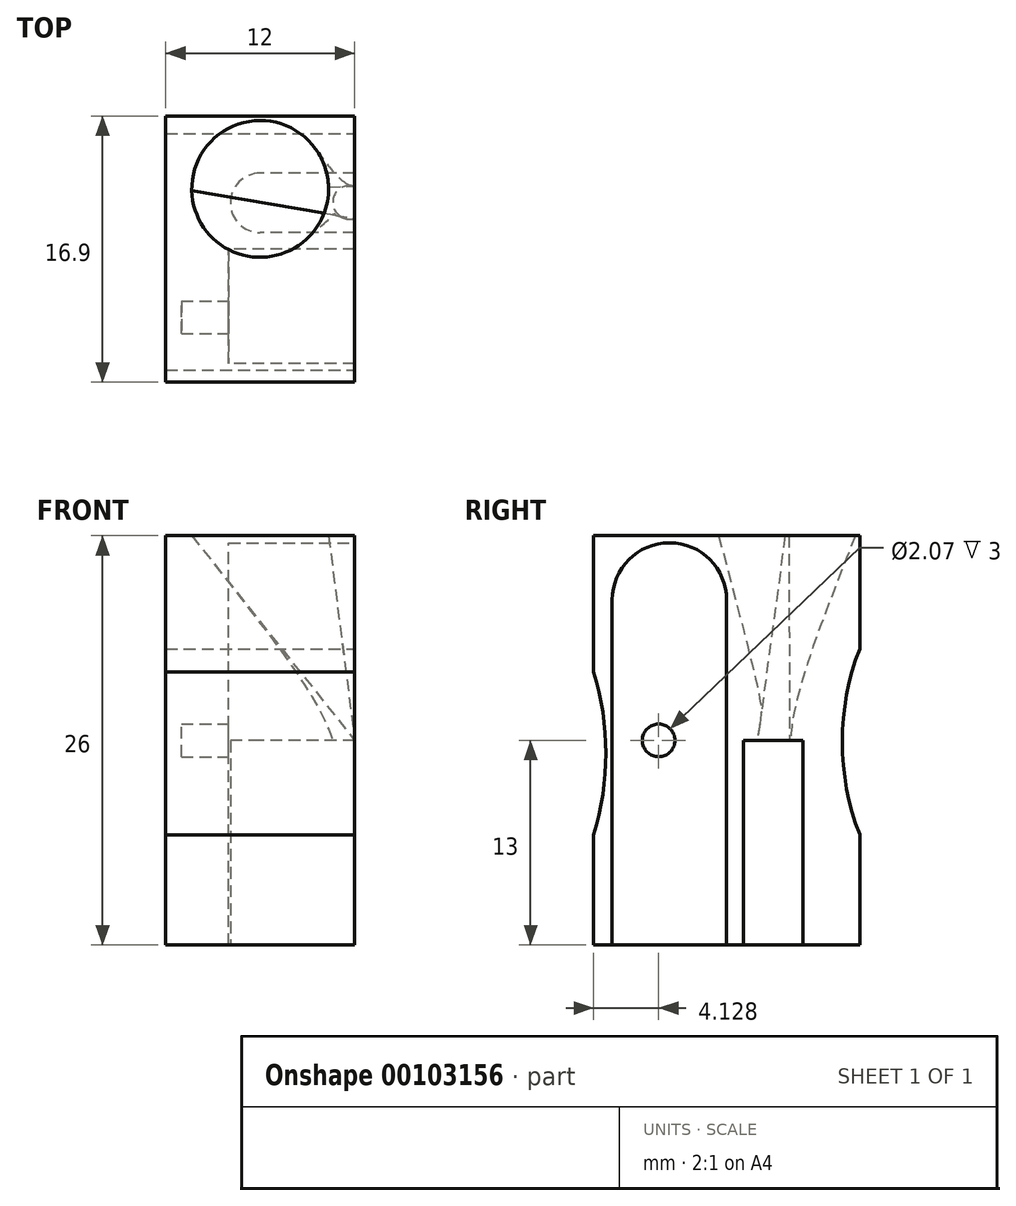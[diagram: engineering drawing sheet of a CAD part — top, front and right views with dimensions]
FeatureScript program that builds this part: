
annotation { "Feature Type Name" : "Feature", "Feature Type Description" : "" }
export const myFeature = defineFeature(function(context is Context, id is Id, definition is map)
    precondition{}
    {
        {
            var Q0;
            Q0=qCreatedBy(makeId("Right.planeOp"),FACE);
            var sketch = newSketch(context, id + "F0", { "sketchPlane" : qUnion([Q0])});
            skLineSegment(sketch, "E0.bottom", {"start": v(-8.45, 13) * mm, "end": v(8.45, 13) * mm});
            skLineSegment(sketch, "E0.top", {"start": v(-8.45, -13) * mm, "end": v(8.45, -13) * mm});
            skLineSegment(sketch, "E0.left", {"start": v(-8.45, 13) * mm, "end": v(-8.45, -13) * mm});
            skLineSegment(sketch, "E0.right", {"start": v(8.45, 13) * mm, "end": v(8.45, -13) * mm});
            skPoint(sketch, "E0.middle", {"position": v(0, 0) * mm});
            skLineSegment(sketch, "E1", {"start": v(0, 0) * mm, "end": v(0, 10.18) * mm});
            skLineSegment(sketch, "E2", {"start": v(6.3, 0) * mm, "end": v(6.3, 10.18) * mm});
            skArc(sketch, "E3", {"start": v(6.3, 10.18) * mm, "mid": v(3.15, 12.07) * mm, "end": v(0, 10.18) * mm});
            skSolve(sketch);
        }
        {
            var Q0;
            Q0=makeQuery(id+"F0.imprint","IMPRINT",FACE,{"disambiguationData":[TD([[makeQuery(id+"F0.imprint","IMPRINT",EDGE,{"derivedFrom":sQuery(id+"F0.wireOp",EDGE,"E0.bottom")}),-1.0]])]});
            extrude(context, id + "F1", {"entities" : qUnion([Q0]), "endBound" : BoundingType.SYMMETRIC, "depth" : 12 * mm});
        }
        {
            var Q0;
            Q0=qCreatedBy(makeId("Right.planeOp"),FACE);
            cPlane(context, id + "F2", {"entities" : qUnion([Q0]), "cplaneType" : CPlaneType.OFFSET, "offset" : 6 * mm, "width" : 150 * mm, "height" : 150 * mm});
        }
        {
            var Q0;
            Q0=qCreatedBy(id+"F2.planeOp",FACE);
            var sketch = newSketch(context, id + "F3", { "sketchPlane" : qUnion([Q0])});
            skLineSegment(sketch, "E4", {"start": v(0, 0) * mm, "end": v(0, 8.92) * mm});
            skLineSegment(sketch, "E5", {"start": v(-7.27, 0) * mm, "end": v(-7.27, 8.92) * mm});
            skArc(sketch, "E6", {"start": v(0, 8.92) * mm, "mid": v(-3.64, 12.55) * mm, "end": v(-7.27, 8.92) * mm});
            skLineSegment(sketch, "E7", {"start": v(-7.27, 0) * mm, "end": v(-7.27, -13.14) * mm});
            skLineSegment(sketch, "E8", {"start": v(-7.27, -13.14) * mm, "end": v(0, -13.14) * mm});
            skLineSegment(sketch, "E9", {"start": v(0, -13.14) * mm, "end": v(0, 0) * mm});
            skSolve(sketch);
        }
        {
            var Q0;
            Q0=makeQuery(id+"F3.imprint","IMPRINT",FACE,{"disambiguationData":[TD([[makeQuery(id+"F3.imprint","IMPRINT",EDGE,{"derivedFrom":sQuery(id+"F3.wireOp",EDGE,"E4")}),1.0]])]});
            extrude(context, id + "F4", {"entities" : qUnion([Q0]), "operationType" : NewBodyOperationType.REMOVE, "oppositeDirection" : true, "depth" : 8 * mm});
        }
        {
            var Q0;
            Q0=qCreatedBy(makeId("Top.planeOp"),FACE);
            cPlane(context, id + "F5", {"entities" : qUnion([Q0]), "cplaneType" : CPlaneType.OFFSET, "offset" : 13 * mm, "oppositeDirection" : true, "width" : 150 * mm, "height" : 150 * mm});
        }
        {
            var Q0;
            Q0=qCreatedBy(id+"F5.planeOp",FACE);
            var sketch = newSketch(context, id + "F6", { "sketchPlane" : qUnion([Q0])});
            skLineSegment(sketch, "E10", {"start": v(6, 1.06) * mm, "end": v(0, 1.06) * mm});
            skLineSegment(sketch, "E11", {"start": v(6, 4.83) * mm, "end": v(0, 4.83) * mm});
            skArc(sketch, "E12", {"start": v(0, 4.83) * mm, "mid": v(-1.89, 2.94) * mm, "end": v(0, 1.06) * mm});
            skLineSegment(sketch, "E13", {"start": v(6, 1.06) * mm, "end": v(6, 4.83) * mm});
            skSolve(sketch);
        }
        {
            var Q0;
            Q0 = qSketchRegion(id + "F6", true);
            extrude(context, id + "F7", {"entities" : qUnion([Q0]), "operationType" : NewBodyOperationType.REMOVE, "depth" : 13 * mm});
        }
        {
            var Q0;
            Q0=qCreatedBy(makeId("Top.planeOp"),FACE);
            var sketch = newSketch(context, id + "F8", { "sketchPlane" : qUnion([Q0])});
            skArc(sketch, "E14", {"start": v(6, 4) * mm, "mid": v(4.62, 2.98) * mm, "end": v(6, 1.96) * mm});
            skLineSegment(sketch, "E15", {"start": v(6, 1.96) * mm, "end": v(6, 4) * mm});
            skSolve(sketch);
        }
        {
            var Q0;
            Q0=qCreatedBy(makeId("Top.planeOp"),FACE);
            cPlane(context, id + "F9", {"entities" : qUnion([Q0]), "cplaneType" : CPlaneType.OFFSET, "offset" : 13 * mm, "width" : 150 * mm, "height" : 150 * mm});
        }
        {
            var Q0;
            Q0=qCreatedBy(id+"F9.planeOp",FACE);
            var sketch = newSketch(context, id + "F10", { "sketchPlane" : qUnion([Q0])});
            skCircle(sketch, "E16", {"center": v(0, 3.83) * mm, "radius": 4.34 * mm});
            skSolve(sketch);
        }
        {
            var Q1;
            Q1 = qSketchRegion(id + "F10", true);
            var Q2;
            Q2 = qSketchRegion(id + "F8", true);
            loft(context, id + "F11", {"operationType" : NewBodyOperationType.REMOVE, "sheetProfilesArray" : [{ "sheetProfileEntities" : qUnion([Q1]) }, { "sheetProfileEntities" : qUnion([Q2]) }]});
        }
        {
            var Q0;
            Q0=qCreatedBy(id+"F2.planeOp",FACE);
            cPlane(context, id + "F12", {"entities" : qUnion([Q0]), "cplaneType" : CPlaneType.OFFSET, "offset" : 8 * mm, "oppositeDirection" : true, "width" : 150 * mm, "height" : 150 * mm});
        }
        {
            var Q0;
            Q0=qCreatedBy(id+"F12.planeOp",FACE);
            var sketch = newSketch(context, id + "F13", { "sketchPlane" : qUnion([Q0])});
            skCircle(sketch, "E17", {"center": v(-4.32, 0) * mm, "radius": 1.04 * mm});
            skSolve(sketch);
        }
        {
            var Q0;
            Q0 = qSketchRegion(id + "F13", true);
            extrude(context, id + "F14", {"entities" : qUnion([Q0]), "operationType" : NewBodyOperationType.REMOVE, "oppositeDirection" : true, "depth" : 3 * mm});
        }
        {
            var Q0;
            Q0=qCreatedBy(id+"F2.planeOp",FACE);
            var sketch = newSketch(context, id + "F15", { "sketchPlane" : qUnion([Q0])});
            skArc(sketch, "E18", {"start": v(8.45, 5.8) * mm, "mid": v(7.34, -0.09) * mm, "end": v(8.45, -5.98) * mm});
            skArc(sketch, "E19", {"start": v(-8.45, -6) * mm, "mid": v(-7.67, -0.82) * mm, "end": v(-8.45, 4.36) * mm});
            skLineSegment(sketch, "E20", {"start": v(8.45, -5.98) * mm, "end": v(8.45, 5.8) * mm});
            skLineSegment(sketch, "E21", {"start": v(-8.45, -6) * mm, "end": v(-8.45, 4.36) * mm});
            skSolve(sketch);
        }
        {
            var Q0;
            Q0 = qSketchRegion(id + "F15", true);
            extrude(context, id + "F16", {"entities" : qUnion([Q0]), "operationType" : NewBodyOperationType.REMOVE, "oppositeDirection" : true, "depth" : 12 * mm});
        }
    });
